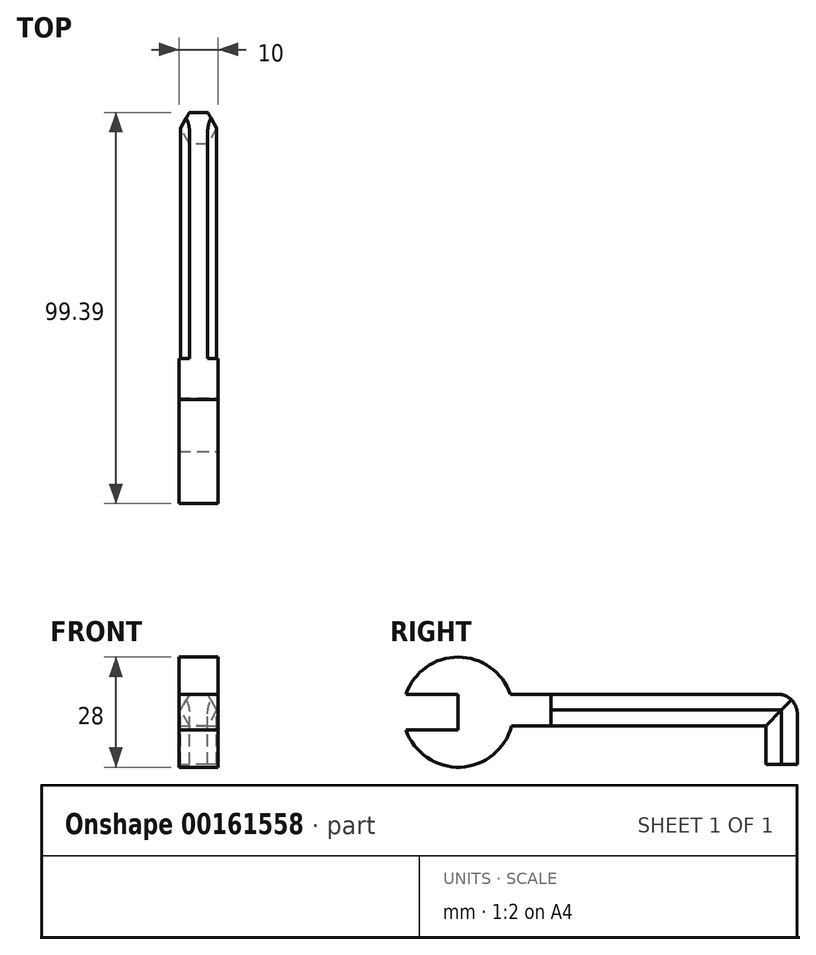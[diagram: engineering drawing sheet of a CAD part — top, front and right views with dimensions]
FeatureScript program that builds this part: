
annotation { "Feature Type Name" : "Feature", "Feature Type Description" : "" }
export const myFeature = defineFeature(function(context is Context, id is Id, definition is map)
    precondition{}
    {
        {
            var Q0;
            Q0=qCreatedBy(makeId("Top.planeOp"),FACE);
            var sketch = newSketch(context, id + "F0", { "sketchPlane" : qUnion([Q0])});
            skCircle(sketch, "E0.cCircle", {"center": v(0, 12.58) * mm, "radius": 4 * mm, "construction": true});
            skLineSegment(sketch, "E0.0", {"start": v(-4.62, 12.58) * mm, "end": v(-2.3, 16.58) * mm});
            skLineSegment(sketch, "E0.1", {"start": v(-2.3, 16.58) * mm, "end": v(2.3, 16.58) * mm});
            skLineSegment(sketch, "E0.2", {"start": v(2.3, 16.58) * mm, "end": v(4.62, 12.58) * mm});
            skLineSegment(sketch, "E0.3", {"start": v(4.62, 12.58) * mm, "end": v(2.3, 8.58) * mm});
            skLineSegment(sketch, "E0.4", {"start": v(2.3, 8.58) * mm, "end": v(-2.3, 8.58) * mm});
            skLineSegment(sketch, "E0.5", {"start": v(-2.3, 8.58) * mm, "end": v(-4.62, 12.58) * mm});
            skPoint(sketch, "E0.0.midPoint", {"position": v(-3.46, 14.58) * mm});
            skSolve(sketch);
        }
        {
            var Q0;
            Q0=qCreatedBy(makeId("Right.planeOp"),FACE);
            var sketch = newSketch(context, id + "F1", { "sketchPlane" : qUnion([Q0])});
            skLineSegment(sketch, "E1", {"start": v(13.74, 0) * mm, "end": v(13.74, 15) * mm});
            skLineSegment(sketch, "E2", {"start": v(13.74, 15) * mm, "end": v(-46.26, 15) * mm});
            skSolve(sketch);
        }
        {
            var Q0;
            Q0=makeQuery(id+"F0.imprint","IMPRINT",FACE,{"disambiguationData":[TD([[makeQuery(id+"F0.imprint","IMPRINT",EDGE,{"derivedFrom":sQuery(id+"F0.wireOp",EDGE,"E0.0")}),-1.0]])]});
            var Q1;
            Q1=sQuery(id+"F1.wireOp",EDGE,"E1");
            var Q2;
            Q2=sQuery(id+"F1.wireOp",EDGE,"E2");
            sweep(context, id + "F2", {"profiles" : qUnion([Q0]), "path" : qUnion([Q1, Q2])});
        }
        {
            var Q0;
            Q0=makeQuery(id+"F2.opSweep","MID_CAP_EDGE",EDGE,{"disambiguationData":[OSD([sQuery(id+"F0.wireOp",EDGE,"E0.1"),sQuery(id+"F1.wireOp",VERTEX,"E2.start")])],"capPos":1.0});
            fillet(context, id + "F3", {"entities" : qUnion([Q0]), "radius" : 5 * mm, "tangentPropagation" : true, "allowEdgeOverflow" : false});
        }
        {
            var Q0;
            Q0=qCreatedBy(makeId("Right.planeOp"),FACE);
            var sketch = newSketch(context, id + "F4", { "sketchPlane" : qUnion([Q0])});
            skLineSegment(sketch, "E3", {"start": v(-82.8, 8.74) * mm, "end": v(-69.57, 8.74) * mm});
            skLineSegment(sketch, "E4", {"start": v(-69.57, 8.74) * mm, "end": v(-69.57, 17.84) * mm});
            skLineSegment(sketch, "E5", {"start": v(-69.57, 17.84) * mm, "end": v(-82.8, 17.84) * mm});
            skPoint(sketch, "E6.center.orphan", {"position": v(-69.57, 13.3) * mm});
            skArc(sketch, "E7", {"start": v(-82.8, 8.74) * mm, "mid": v(-69, -0.7) * mm, "end": v(-56, 9.84) * mm});
            skLineSegment(sketch, "E8.bottom", {"start": v(-56, 9.84) * mm, "end": v(-46, 9.84) * mm});
            skLineSegment(sketch, "E8.top", {"start": v(-56.33, 17.84) * mm, "end": v(-46, 17.84) * mm});
            skLineSegment(sketch, "E8.right", {"start": v(-46, 9.84) * mm, "end": v(-46, 17.84) * mm});
            skArc(sketch, "E9.trimOffspring", {"start": v(-56.33, 17.84) * mm, "mid": v(-69.57, 27.3) * mm, "end": v(-82.8, 17.84) * mm});
            skSolve(sketch);
        }
        {
            var Q0;
            Q0 = qSketchRegion(id + "F4", true);
            extrude(context, id + "F5", {"entities" : qUnion([Q0]), "operationType" : NewBodyOperationType.ADD, "endBound" : BoundingType.SYMMETRIC, "oppositeDirection" : true, "depth" : 10 * mm});
        }
    });
